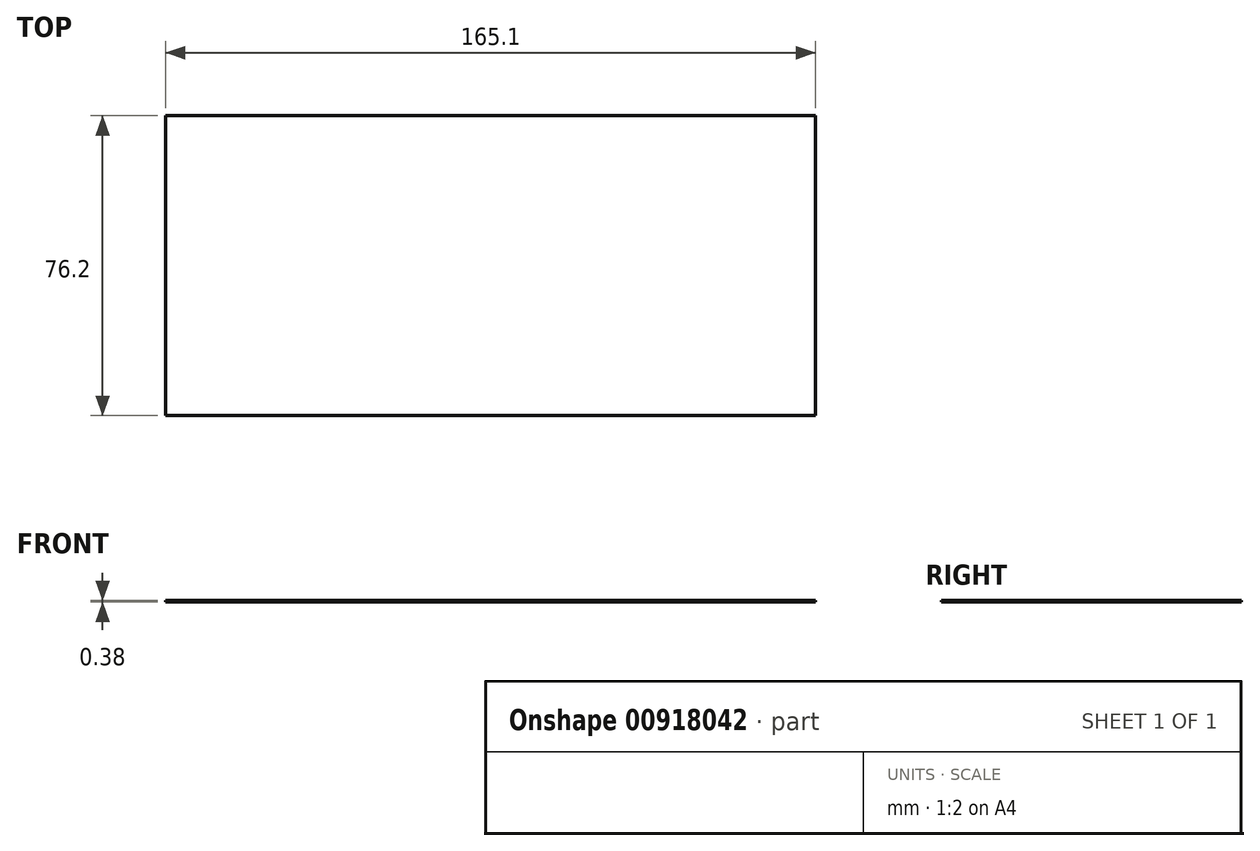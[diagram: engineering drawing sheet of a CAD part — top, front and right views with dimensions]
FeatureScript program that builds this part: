
annotation { "Feature Type Name" : "Feature", "Feature Type Description" : "" }
export const myFeature = defineFeature(function(context is Context, id is Id, definition is map)
    precondition{}
    {
        {
            var Q0;
            Q0=qCreatedBy(makeId("Top.planeOp"),FACE);
            var sketch = newSketch(context, id + "F0", { "sketchPlane" : qUnion([Q0])});
            skLineSegment(sketch, "E0.bottom", {"start": v(-68.77, 35.74) * mm, "end": v(96.33, 35.74) * mm});
            skLineSegment(sketch, "E0.top", {"start": v(-68.77, -40.46) * mm, "end": v(96.33, -40.46) * mm});
            skLineSegment(sketch, "E0.left", {"start": v(-68.77, 35.74) * mm, "end": v(-68.77, -40.46) * mm});
            skLineSegment(sketch, "E0.right", {"start": v(96.33, 35.74) * mm, "end": v(96.33, -40.46) * mm});
            skSolve(sketch);
        }
        {
            var Q0;
            Q0=makeQuery(id+"F0.imprint","IMPRINT",FACE,{"disambiguationData":[TD([[makeQuery(id+"F0.imprint","IMPRINT",EDGE,{"derivedFrom":sQuery(id+"F0.wireOp",EDGE,"E0.bottom")}),-1.0]])]});
            extrude(context, id + "F1", {"entities" : qUnion([Q0]), "depth" : 0.38 * mm, "offsetDistance" : 25.4 * mm});
        }
    });
